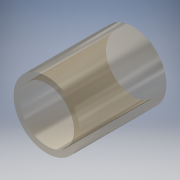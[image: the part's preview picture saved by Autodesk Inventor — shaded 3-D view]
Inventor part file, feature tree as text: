
AUTODESK INVENTOR PART (.ipt)
format: ipt  version: 2017 (Build 210142000, 142)  size: 108,544 bytes
history: native  units: in
note: dims shown in document units (in); Inventor stores cm internally (conversion verified against a paired STEP export)
features: other x2, extrude x1, sketch x1, reference x1
ambient origin geometry x8: Origin, YZ Plane, XZ Plane, XY Plane, X Axis, Y Axis, Z Axis, Center Point
bodies: Solid1 (feature_tree)
feature tree (5):
  extrude  "Extrusion1"  Depth=0.4in TaperAngle=0.0deg
  sketch  "Sketch1"  dims[d0=0.002in d1=0.4in d2=0.0in]
  reference  "Reference1"
  other  "Joule Heating-bnk.iam"
  other  "Al Rod Height A Cooling_1"
